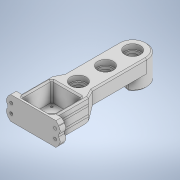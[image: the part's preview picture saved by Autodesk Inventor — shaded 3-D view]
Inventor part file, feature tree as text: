
AUTODESK INVENTOR PART (.ipt)
format: ipt  version: 2021 (Build 250183000, 183)  size: 584,192 bytes
history: native  units: mm
features: extrude x14, sketch x14, chamfer x10, plane x1, fillet x1
ambient origin geometry x8: Origin, YZ Plane, XZ Plane, XY Plane, X Axis, Y Axis, Z Axis, Center Point
bodies: Solid1 (feature_tree)
feature tree (40):
  extrude  "Extrusion1"  Depth=22.3mm
  plane  "Work Plane1"
  extrude  "Extrusion3"  Depth=38.5mm
  extrude  "Extrusion4"  Depth=40.0mm
  chamfer  "Chamfer2"  Distance=21.0mm
  extrude  "Extrusion2"  Depth=14.0mm
  extrude  "Extrusion5"  Depth=7.0mm TaperAngle=0.0deg
  extrude  "Extrusion6"  Depth=42.2mm
  chamfer  "Chamfer4"  Distance=7.0mm
  chamfer  "Chamfer5"  Distance=3.2mm
  chamfer  "Chamfer7"  Distance=3.2mm
  extrude  "Extrusion10"  Depth=7.0mm
  chamfer  "Chamfer10"  Distance=31.5mm
  extrude  "Extrusion11"  Depth=7.0mm
  extrude  "Extrusion14"  Depth=7.0mm
  sketch  "Sketch16"  dims[d21=0.0mm]
  chamfer  "Chamfer13"  Distance=5.35mm
  extrude  "Extrusion15"  Depth=7.0mm
  fillet  "Fillet4"  Radius=5.35mm
  chamfer  "Chamfer14"  Distance=5.35mm
  extrude  "Extrusion16"  Depth=23.0mm
  chamfer  "Chamfer16"  Distance=21.1mm
  extrude  "Extrusion17"  Depth=7.0mm
  extrude  "Extrusion18"  Depth=7.0mm TaperAngle=0.0deg
  chamfer  "Chamfer17"  Distance=11.9mm Angle=45.0deg
  extrude  "Extrusion19"  Depth=7.0mm
  chamfer  "Chamfer18"  Distance=4.2mm
  sketch  "Sketch1"  dims[d0=22.3mm d1=22.3mm]
  sketch  "Sketch2"  dims[d2=0.0mm d3=38.5mm]
  sketch  "Sketch3"  dims[d4=40.0mm d5=40.0mm d6=21.0mm d7=0.0mm]
  sketch  "Sketch4"  dims[d8=-7.0mm d9=14.0mm]
  sketch  "Sketch5"  dims[d10=14.0mm d11=7.0mm d12=0.0mm]
  sketch  "Sketch6"  dims[d16=42.2mm d17=42.2mm]
  sketch  "Sketch11"  dims[d18=21.1mm]
  sketch  "Sketch12"  dims[d19=21.1mm]
  sketch  "Sketch15"  dims[d20=23.0mm]
  sketch  "Sketch17"  dims[d22=38.0mm]
  sketch  "Sketch18"  dims[d23=5.0mm d24=7.0mm d25=0.0mm]
  sketch  "Sketch19"  dims[d26=3.2mm]
  sketch  "Sketch20"  dims[d27=3.2mm d28=3.2mm d29=3.2mm d30=31.5mm d31=31.5mm d32=31.5mm d33=31.5mm d34=5.35mm d35=5.35mm d36=5.35mm d37=5.35mm d38=23.0mm d39=21.1mm d40=21.1mm d41=5.0mm d42=0.0mm d43=11.9mm d44=2.0mm d45=45.0deg d47=4.2mm d48=4.2mm d52=10.0mm d54=4.2mm d55=4.2mm d59=10.0mm d60=8.0mm d61=0.0mm d62=10.0mm d63=10.0mm d64=10.0mm d65=10.0mm d66=4.0mm d67=0.0mm d71=1.5mm d72=2.0mm d73=45.0deg d74=0.1mm d75=2.0mm d76=45.0deg d93=2.0mm d94=2.0mm d95=45.0deg d105=0.25mm d106=0.25mm d107=0.25mm d108=0.25mm d109=7.0mm d110=0.0mm d111=2.0mm d112=2.0mm d113=45.0deg d114=7.0mm d115=0.0mm d129=22.3mm d130=40.0mm d132=38.5mm d133=10.2mm d134=10.2mm d135=10.2mm d136=10.2mm d137=4.2mm d138=4.2mm d139=4.2mm d140=4.2mm d141=4.0mm d142=0.0mm d146=4.2mm d147=4.2mm d148=4.2mm d149=4.2mm d150=10.0mm d151=10.0mm d152=5.0mm d153=5.0mm d154=5.0005mm d155=5.0005mm d156=10.0mm d157=10.0mm d158=14.0mm d159=14.0mm d160=14.0mm d161=14.0mm d162=4.0mm d163=2.0mm d164=45.0deg d165=4.0mm d166=0.0mm d167=15.0mm d168=14.0mm d169=2.0mm d170=2.0mm d171=45.0deg d175=10.5mm d176=10.5mm d177=10.5mm d178=10.5mm d179=50.0mm d180=0.0mm d181=2.0mm d182=2.0mm d183=45.0deg d184=14.0mm d185=40.0mm d186=16.0mm d187=8.0mm d188=0.0mm d189=0.0mm d190=22.3mm d191=7.0mm d192=0.0mm d193=2.0mm d194=2.0mm d195=45.0deg d196=46.0mm d197=16.0mm d198=0.0mm d199=2.0mm d200=2.0mm d201=45.0deg]
